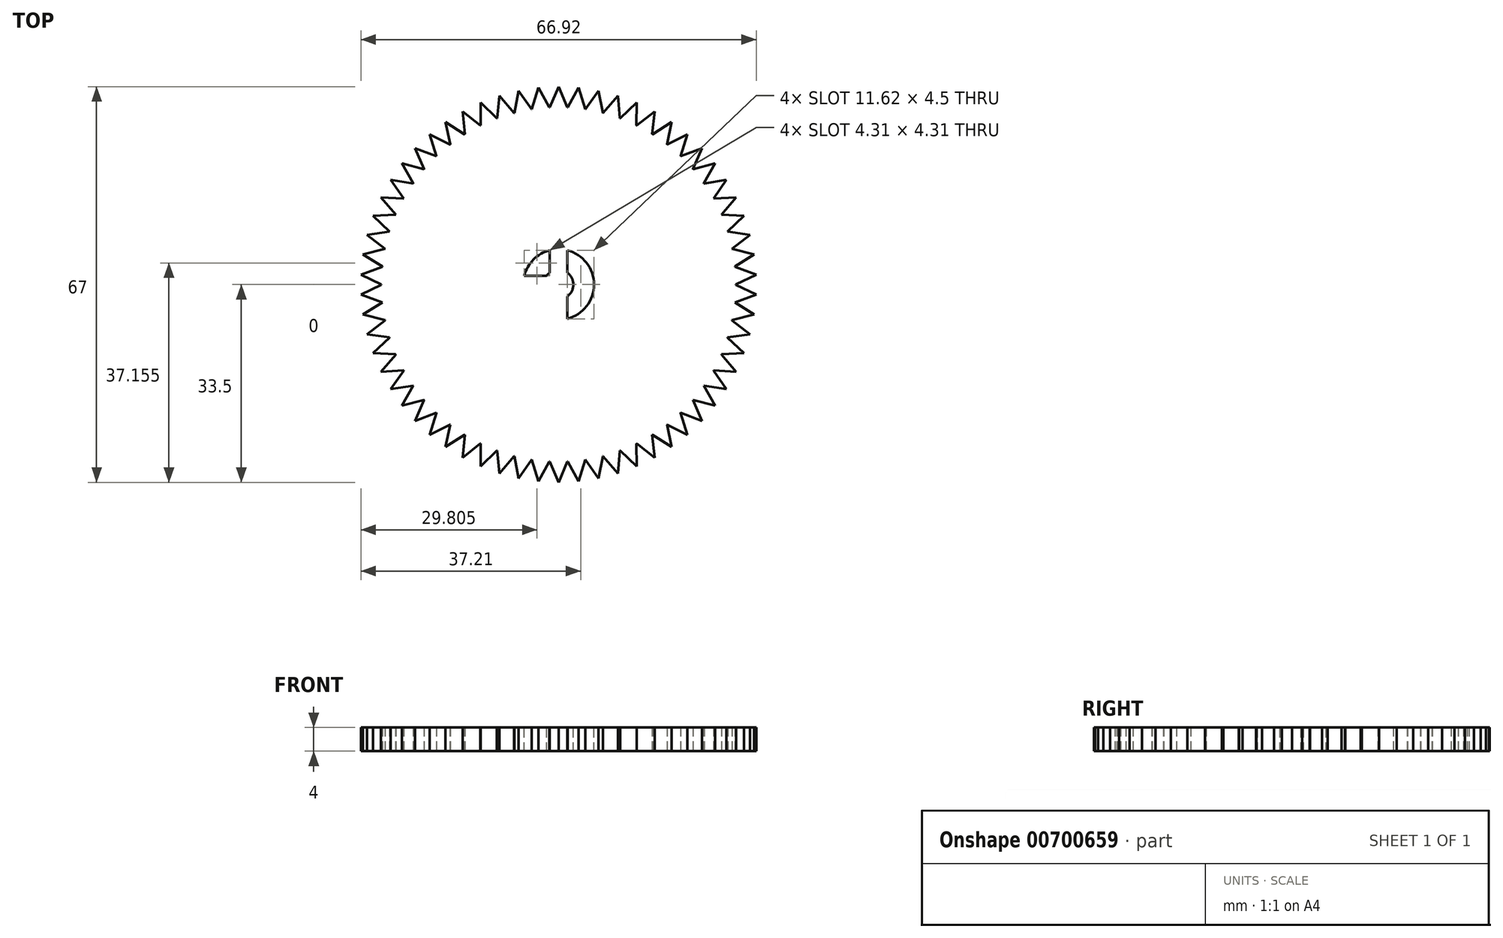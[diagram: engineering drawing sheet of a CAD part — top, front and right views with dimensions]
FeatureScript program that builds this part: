
annotation { "Feature Type Name" : "Feature", "Feature Type Description" : "" }
export const myFeature = defineFeature(function(context is Context, id is Id, definition is map)
    precondition{}
    {
        {
            var Q0;
            Q0=qCreatedBy(makeId("Top.planeOp"),FACE);
            var sketch = newSketch(context, id + "F0", { "sketchPlane" : qUnion([Q0])});
            skCircle(sketch, "E0", {"center": v(0, 0) * mm, "radius": 30 * mm});
            skLineSegment(sketch, "E1", {"start": v(0, 33.5) * mm, "end": v(-1.5, 29.96) * mm});
            skLineSegment(sketch, "E2", {"start": v(0, 33.5) * mm, "end": v(1.5, 29.96) * mm});
            skLineSegment(sketch, "E3.1.0", {"start": v(-3.39, 33.33) * mm, "end": v(-4.52, 29.66) * mm});
            skLineSegment(sketch, "E3.1.1", {"start": v(-3.39, 33.33) * mm, "end": v(-1.54, 29.96) * mm});
            skLineSegment(sketch, "E3.2.0", {"start": v(-6.74, 32.81) * mm, "end": v(-7.5, 29.05) * mm});
            skLineSegment(sketch, "E3.2.1", {"start": v(-6.74, 32.81) * mm, "end": v(-4.56, 29.65) * mm});
            skLineSegment(sketch, "E3.3.0", {"start": v(-10.03, 31.96) * mm, "end": v(-10.4, 28.14) * mm});
            skLineSegment(sketch, "E3.3.1", {"start": v(-10.03, 31.96) * mm, "end": v(-7.54, 29.04) * mm});
            skLineSegment(sketch, "E3.4.0", {"start": v(-13.21, 30.79) * mm, "end": v(-13.2, 26.94) * mm});
            skLineSegment(sketch, "E3.4.1", {"start": v(-13.21, 30.79) * mm, "end": v(-10.44, 28.13) * mm});
            skLineSegment(sketch, "E3.5.0", {"start": v(-16.26, 29.3) * mm, "end": v(-15.85, 25.47) * mm});
            skLineSegment(sketch, "E3.5.1", {"start": v(-16.26, 29.3) * mm, "end": v(-13.23, 26.93) * mm});
            skLineSegment(sketch, "E3.6.0", {"start": v(-19.14, 27.5) * mm, "end": v(-18.35, 23.74) * mm});
            skLineSegment(sketch, "E3.6.1", {"start": v(-19.14, 27.5) * mm, "end": v(-15.89, 25.45) * mm});
            skLineSegment(sketch, "E3.7.0", {"start": v(-21.82, 25.42) * mm, "end": v(-20.65, 21.76) * mm});
            skLineSegment(sketch, "E3.7.1", {"start": v(-21.82, 25.42) * mm, "end": v(-18.38, 23.71) * mm});
            skLineSegment(sketch, "E3.8.0", {"start": v(-24.28, 23.08) * mm, "end": v(-22.75, 19.56) * mm});
            skLineSegment(sketch, "E3.8.1", {"start": v(-24.28, 23.08) * mm, "end": v(-20.68, 21.73) * mm});
            skLineSegment(sketch, "E3.9.0", {"start": v(-26.5, 20.5) * mm, "end": v(-24.61, 17.15) * mm});
            skLineSegment(sketch, "E3.9.1", {"start": v(-26.5, 20.5) * mm, "end": v(-22.78, 19.53) * mm});
            skLineSegment(sketch, "E3.10.0", {"start": v(-28.43, 17.72) * mm, "end": v(-26.22, 14.58) * mm});
            skLineSegment(sketch, "E3.10.1", {"start": v(-28.43, 17.72) * mm, "end": v(-24.63, 17.12) * mm});
            skLineSegment(sketch, "E3.11.0", {"start": v(-30.08, 14.75) * mm, "end": v(-27.56, 11.85) * mm});
            skLineSegment(sketch, "E3.11.1", {"start": v(-30.08, 14.75) * mm, "end": v(-26.24, 14.54) * mm});
            skLineSegment(sketch, "E3.12.0", {"start": v(-31.41, 11.63) * mm, "end": v(-28.62, 9) * mm});
            skLineSegment(sketch, "E3.12.1", {"start": v(-31.41, 11.63) * mm, "end": v(-27.58, 11.81) * mm});
            skLineSegment(sketch, "E3.13.0", {"start": v(-32.43, 8.4) * mm, "end": v(-29.38, 6.06) * mm});
            skLineSegment(sketch, "E3.13.1", {"start": v(-32.43, 8.4) * mm, "end": v(-28.63, 8.96) * mm});
            skLineSegment(sketch, "E3.14.0", {"start": v(-33.11, 5.07) * mm, "end": v(-29.84, 3.05) * mm});
            skLineSegment(sketch, "E3.14.1", {"start": v(-33.11, 5.07) * mm, "end": v(-29.39, 6.02) * mm});
            skLineSegment(sketch, "E3.15.0", {"start": v(-33.46, 1.7) * mm, "end": v(-30, 0.02) * mm});
            skLineSegment(sketch, "E3.15.1", {"start": v(-33.46, 1.7) * mm, "end": v(-29.85, 3.02) * mm});
            skLineSegment(sketch, "E3.16.0", {"start": v(-33.46, -1.7) * mm, "end": v(-29.85, -3.02) * mm});
            skLineSegment(sketch, "E3.16.1", {"start": v(-33.46, -1.7) * mm, "end": v(-30, -0.02) * mm});
            skLineSegment(sketch, "E3.17.0", {"start": v(-33.11, -5.07) * mm, "end": v(-29.39, -6.02) * mm});
            skLineSegment(sketch, "E3.17.1", {"start": v(-33.11, -5.07) * mm, "end": v(-29.84, -3.05) * mm});
            skLineSegment(sketch, "E3.18.0", {"start": v(-32.43, -8.4) * mm, "end": v(-28.63, -8.96) * mm});
            skLineSegment(sketch, "E3.18.1", {"start": v(-32.43, -8.4) * mm, "end": v(-29.38, -6.06) * mm});
            skLineSegment(sketch, "E3.19.0", {"start": v(-31.41, -11.63) * mm, "end": v(-27.58, -11.81) * mm});
            skLineSegment(sketch, "E3.19.1", {"start": v(-31.41, -11.63) * mm, "end": v(-28.62, -9) * mm});
            skLineSegment(sketch, "E3.20.0", {"start": v(-30.08, -14.75) * mm, "end": v(-26.24, -14.54) * mm});
            skLineSegment(sketch, "E3.20.1", {"start": v(-30.08, -14.75) * mm, "end": v(-27.56, -11.85) * mm});
            skLineSegment(sketch, "E3.21.0", {"start": v(-28.43, -17.72) * mm, "end": v(-24.63, -17.12) * mm});
            skLineSegment(sketch, "E3.21.1", {"start": v(-28.43, -17.72) * mm, "end": v(-26.22, -14.58) * mm});
            skLineSegment(sketch, "E3.22.0", {"start": v(-26.5, -20.5) * mm, "end": v(-22.78, -19.53) * mm});
            skLineSegment(sketch, "E3.22.1", {"start": v(-26.5, -20.5) * mm, "end": v(-24.61, -17.15) * mm});
            skLineSegment(sketch, "E3.23.0", {"start": v(-24.28, -23.08) * mm, "end": v(-20.68, -21.73) * mm});
            skLineSegment(sketch, "E3.23.1", {"start": v(-24.28, -23.08) * mm, "end": v(-22.75, -19.56) * mm});
            skLineSegment(sketch, "E3.24.0", {"start": v(-21.82, -25.42) * mm, "end": v(-18.38, -23.71) * mm});
            skLineSegment(sketch, "E3.24.1", {"start": v(-21.82, -25.42) * mm, "end": v(-20.65, -21.76) * mm});
            skLineSegment(sketch, "E3.25.0", {"start": v(-19.14, -27.5) * mm, "end": v(-15.89, -25.45) * mm});
            skLineSegment(sketch, "E3.25.1", {"start": v(-19.14, -27.5) * mm, "end": v(-18.35, -23.74) * mm});
            skLineSegment(sketch, "E3.26.0", {"start": v(-16.26, -29.3) * mm, "end": v(-13.23, -26.93) * mm});
            skLineSegment(sketch, "E3.26.1", {"start": v(-16.26, -29.3) * mm, "end": v(-15.85, -25.47) * mm});
            skLineSegment(sketch, "E3.27.0", {"start": v(-13.21, -30.79) * mm, "end": v(-10.44, -28.13) * mm});
            skLineSegment(sketch, "E3.27.1", {"start": v(-13.21, -30.79) * mm, "end": v(-13.2, -26.94) * mm});
            skLineSegment(sketch, "E3.28.0", {"start": v(-10.03, -31.96) * mm, "end": v(-7.54, -29.04) * mm});
            skLineSegment(sketch, "E3.28.1", {"start": v(-10.03, -31.96) * mm, "end": v(-10.4, -28.14) * mm});
            skLineSegment(sketch, "E3.29.0", {"start": v(-6.74, -32.81) * mm, "end": v(-4.56, -29.65) * mm});
            skLineSegment(sketch, "E3.29.1", {"start": v(-6.74, -32.81) * mm, "end": v(-7.5, -29.05) * mm});
            skLineSegment(sketch, "E3.30.0", {"start": v(-3.39, -33.33) * mm, "end": v(-1.54, -29.96) * mm});
            skLineSegment(sketch, "E3.30.1", {"start": v(-3.39, -33.33) * mm, "end": v(-4.52, -29.66) * mm});
            skLineSegment(sketch, "E3.31.0", {"start": v(0, -33.5) * mm, "end": v(1.5, -29.96) * mm});
            skLineSegment(sketch, "E3.31.1", {"start": v(0, -33.5) * mm, "end": v(-1.5, -29.96) * mm});
            skLineSegment(sketch, "E3.32.0", {"start": v(3.39, -33.33) * mm, "end": v(4.52, -29.66) * mm});
            skLineSegment(sketch, "E3.32.1", {"start": v(3.39, -33.33) * mm, "end": v(1.54, -29.96) * mm});
            skLineSegment(sketch, "E3.33.0", {"start": v(6.74, -32.81) * mm, "end": v(7.5, -29.05) * mm});
            skLineSegment(sketch, "E3.33.1", {"start": v(6.74, -32.81) * mm, "end": v(4.56, -29.65) * mm});
            skLineSegment(sketch, "E3.34.0", {"start": v(10.03, -31.96) * mm, "end": v(10.4, -28.14) * mm});
            skLineSegment(sketch, "E3.34.1", {"start": v(10.03, -31.96) * mm, "end": v(7.54, -29.04) * mm});
            skLineSegment(sketch, "E3.35.0", {"start": v(13.21, -30.79) * mm, "end": v(13.2, -26.94) * mm});
            skLineSegment(sketch, "E3.35.1", {"start": v(13.21, -30.79) * mm, "end": v(10.44, -28.13) * mm});
            skLineSegment(sketch, "E3.36.0", {"start": v(16.26, -29.3) * mm, "end": v(15.85, -25.47) * mm});
            skLineSegment(sketch, "E3.36.1", {"start": v(16.26, -29.3) * mm, "end": v(13.23, -26.93) * mm});
            skLineSegment(sketch, "E3.37.0", {"start": v(19.14, -27.5) * mm, "end": v(18.35, -23.74) * mm});
            skLineSegment(sketch, "E3.37.1", {"start": v(19.14, -27.5) * mm, "end": v(15.89, -25.45) * mm});
            skLineSegment(sketch, "E3.38.0", {"start": v(21.82, -25.42) * mm, "end": v(20.65, -21.76) * mm});
            skLineSegment(sketch, "E3.38.1", {"start": v(21.82, -25.42) * mm, "end": v(18.38, -23.71) * mm});
            skLineSegment(sketch, "E3.39.0", {"start": v(24.28, -23.08) * mm, "end": v(22.75, -19.56) * mm});
            skLineSegment(sketch, "E3.39.1", {"start": v(24.28, -23.08) * mm, "end": v(20.68, -21.73) * mm});
            skLineSegment(sketch, "E3.40.0", {"start": v(26.5, -20.5) * mm, "end": v(24.61, -17.15) * mm});
            skLineSegment(sketch, "E3.40.1", {"start": v(26.5, -20.5) * mm, "end": v(22.78, -19.53) * mm});
            skLineSegment(sketch, "E3.41.0", {"start": v(28.43, -17.72) * mm, "end": v(26.22, -14.58) * mm});
            skLineSegment(sketch, "E3.41.1", {"start": v(28.43, -17.72) * mm, "end": v(24.63, -17.12) * mm});
            skLineSegment(sketch, "E3.42.0", {"start": v(30.08, -14.75) * mm, "end": v(27.56, -11.85) * mm});
            skLineSegment(sketch, "E3.42.1", {"start": v(30.08, -14.75) * mm, "end": v(26.24, -14.54) * mm});
            skLineSegment(sketch, "E3.43.0", {"start": v(31.41, -11.63) * mm, "end": v(28.62, -9) * mm});
            skLineSegment(sketch, "E3.43.1", {"start": v(31.41, -11.63) * mm, "end": v(27.58, -11.81) * mm});
            skLineSegment(sketch, "E3.44.0", {"start": v(32.43, -8.4) * mm, "end": v(29.38, -6.06) * mm});
            skLineSegment(sketch, "E3.44.1", {"start": v(32.43, -8.4) * mm, "end": v(28.63, -8.96) * mm});
            skLineSegment(sketch, "E3.45.0", {"start": v(33.11, -5.07) * mm, "end": v(29.84, -3.05) * mm});
            skLineSegment(sketch, "E3.45.1", {"start": v(33.11, -5.07) * mm, "end": v(29.39, -6.02) * mm});
            skLineSegment(sketch, "E3.46.0", {"start": v(33.46, -1.7) * mm, "end": v(30, -0.02) * mm});
            skLineSegment(sketch, "E3.46.1", {"start": v(33.46, -1.7) * mm, "end": v(29.85, -3.02) * mm});
            skLineSegment(sketch, "E3.47.0", {"start": v(33.46, 1.7) * mm, "end": v(29.85, 3.02) * mm});
            skLineSegment(sketch, "E3.47.1", {"start": v(33.46, 1.7) * mm, "end": v(30, 0.02) * mm});
            skLineSegment(sketch, "E3.48.0", {"start": v(33.11, 5.07) * mm, "end": v(29.39, 6.02) * mm});
            skLineSegment(sketch, "E3.48.1", {"start": v(33.11, 5.07) * mm, "end": v(29.84, 3.05) * mm});
            skLineSegment(sketch, "E3.49.0", {"start": v(32.43, 8.4) * mm, "end": v(28.63, 8.96) * mm});
            skLineSegment(sketch, "E3.49.1", {"start": v(32.43, 8.4) * mm, "end": v(29.38, 6.06) * mm});
            skLineSegment(sketch, "E3.50.0", {"start": v(31.41, 11.63) * mm, "end": v(27.58, 11.81) * mm});
            skLineSegment(sketch, "E3.50.1", {"start": v(31.41, 11.63) * mm, "end": v(28.62, 9) * mm});
            skLineSegment(sketch, "E3.51.0", {"start": v(30.08, 14.75) * mm, "end": v(26.24, 14.54) * mm});
            skLineSegment(sketch, "E3.51.1", {"start": v(30.08, 14.75) * mm, "end": v(27.56, 11.85) * mm});
            skLineSegment(sketch, "E3.52.0", {"start": v(28.43, 17.72) * mm, "end": v(24.63, 17.12) * mm});
            skLineSegment(sketch, "E3.52.1", {"start": v(28.43, 17.72) * mm, "end": v(26.22, 14.58) * mm});
            skLineSegment(sketch, "E3.53.0", {"start": v(26.5, 20.5) * mm, "end": v(22.78, 19.53) * mm});
            skLineSegment(sketch, "E3.53.1", {"start": v(26.5, 20.5) * mm, "end": v(24.61, 17.15) * mm});
            skLineSegment(sketch, "E3.54.0", {"start": v(24.28, 23.08) * mm, "end": v(20.68, 21.73) * mm});
            skLineSegment(sketch, "E3.54.1", {"start": v(24.28, 23.08) * mm, "end": v(22.75, 19.56) * mm});
            skLineSegment(sketch, "E3.55.0", {"start": v(21.82, 25.42) * mm, "end": v(18.38, 23.71) * mm});
            skLineSegment(sketch, "E3.55.1", {"start": v(21.82, 25.42) * mm, "end": v(20.65, 21.76) * mm});
            skLineSegment(sketch, "E3.56.0", {"start": v(19.14, 27.5) * mm, "end": v(15.89, 25.45) * mm});
            skLineSegment(sketch, "E3.56.1", {"start": v(19.14, 27.5) * mm, "end": v(18.35, 23.74) * mm});
            skLineSegment(sketch, "E3.57.0", {"start": v(16.26, 29.3) * mm, "end": v(13.23, 26.93) * mm});
            skLineSegment(sketch, "E3.57.1", {"start": v(16.26, 29.3) * mm, "end": v(15.85, 25.47) * mm});
            skLineSegment(sketch, "E3.58.0", {"start": v(13.21, 30.79) * mm, "end": v(10.44, 28.13) * mm});
            skLineSegment(sketch, "E3.58.1", {"start": v(13.21, 30.79) * mm, "end": v(13.2, 26.94) * mm});
            skLineSegment(sketch, "E3.59.0", {"start": v(10.03, 31.96) * mm, "end": v(7.54, 29.04) * mm});
            skLineSegment(sketch, "E3.59.1", {"start": v(10.03, 31.96) * mm, "end": v(10.4, 28.14) * mm});
            skLineSegment(sketch, "E3.60.0", {"start": v(6.74, 32.81) * mm, "end": v(4.56, 29.65) * mm});
            skLineSegment(sketch, "E3.60.1", {"start": v(6.74, 32.81) * mm, "end": v(7.5, 29.05) * mm});
            skLineSegment(sketch, "E3.61.0", {"start": v(3.39, 33.33) * mm, "end": v(1.54, 29.96) * mm});
            skLineSegment(sketch, "E3.61.1", {"start": v(3.39, 33.33) * mm, "end": v(4.52, 29.66) * mm});
            skSolve(sketch);
        }
        {
            var Q0;
            Q0 = qSketchRegion(id + "F0", true);
            extrude(context, id + "F1", {"entities" : qUnion([Q0]), "depth" : 4 * mm, "offsetDistance" : 25 * mm});
        }
        {
            var Q0;
            Q0=makeQuery(id+"F1.opExtrude","CAP_FACE",FACE,{"disambiguationData":[OSD([sQuery(id+"F0.wireOp",EDGE,"E0"),sQuery(id+"F0.wireOp",EDGE,"E1"),sQuery(id+"F0.wireOp",EDGE,"E2"),sQuery(id+"F0.wireOp",EDGE,"E3.1.0"),sQuery(id+"F0.wireOp",EDGE,"E3.1.1"),sQuery(id+"F0.wireOp",EDGE,"E3.2.0"),sQuery(id+"F0.wireOp",EDGE,"E3.2.1"),sQuery(id+"F0.wireOp",EDGE,"E3.3.0"),sQuery(id+"F0.wireOp",EDGE,"E3.3.1"),sQuery(id+"F0.wireOp",EDGE,"E3.4.0"),sQuery(id+"F0.wireOp",EDGE,"E3.4.1"),sQuery(id+"F0.wireOp",EDGE,"E3.5.0"),sQuery(id+"F0.wireOp",EDGE,"E3.5.1"),sQuery(id+"F0.wireOp",EDGE,"E3.6.0"),sQuery(id+"F0.wireOp",EDGE,"E3.6.1"),sQuery(id+"F0.wireOp",EDGE,"E3.7.0"),sQuery(id+"F0.wireOp",EDGE,"E3.7.1"),sQuery(id+"F0.wireOp",EDGE,"E3.8.0"),sQuery(id+"F0.wireOp",EDGE,"E3.8.1"),sQuery(id+"F0.wireOp",EDGE,"E3.9.0"),sQuery(id+"F0.wireOp",EDGE,"E3.9.1"),sQuery(id+"F0.wireOp",EDGE,"E3.10.0"),sQuery(id+"F0.wireOp",EDGE,"E3.10.1"),sQuery(id+"F0.wireOp",EDGE,"E3.11.0"),sQuery(id+"F0.wireOp",EDGE,"E3.11.1"),sQuery(id+"F0.wireOp",EDGE,"E3.12.0"),sQuery(id+"F0.wireOp",EDGE,"E3.12.1"),sQuery(id+"F0.wireOp",EDGE,"E3.13.0"),sQuery(id+"F0.wireOp",EDGE,"E3.13.1"),sQuery(id+"F0.wireOp",EDGE,"E3.14.0"),sQuery(id+"F0.wireOp",EDGE,"E3.14.1"),sQuery(id+"F0.wireOp",EDGE,"E3.15.0"),sQuery(id+"F0.wireOp",EDGE,"E3.15.1"),sQuery(id+"F0.wireOp",EDGE,"E3.16.0"),sQuery(id+"F0.wireOp",EDGE,"E3.16.1"),sQuery(id+"F0.wireOp",EDGE,"E3.17.0"),sQuery(id+"F0.wireOp",EDGE,"E3.17.1"),sQuery(id+"F0.wireOp",EDGE,"E3.18.0"),sQuery(id+"F0.wireOp",EDGE,"E3.18.1"),sQuery(id+"F0.wireOp",EDGE,"E3.19.0"),sQuery(id+"F0.wireOp",EDGE,"E3.19.1"),sQuery(id+"F0.wireOp",EDGE,"E3.20.0"),sQuery(id+"F0.wireOp",EDGE,"E3.20.1"),sQuery(id+"F0.wireOp",EDGE,"E3.21.0"),sQuery(id+"F0.wireOp",EDGE,"E3.21.1"),sQuery(id+"F0.wireOp",EDGE,"E3.22.0"),sQuery(id+"F0.wireOp",EDGE,"E3.22.1"),sQuery(id+"F0.wireOp",EDGE,"E3.23.0"),sQuery(id+"F0.wireOp",EDGE,"E3.23.1"),sQuery(id+"F0.wireOp",EDGE,"E3.24.0"),sQuery(id+"F0.wireOp",EDGE,"E3.24.1"),sQuery(id+"F0.wireOp",EDGE,"E3.25.0"),sQuery(id+"F0.wireOp",EDGE,"E3.25.1"),sQuery(id+"F0.wireOp",EDGE,"E3.26.0"),sQuery(id+"F0.wireOp",EDGE,"E3.26.1"),sQuery(id+"F0.wireOp",EDGE,"E3.27.0"),sQuery(id+"F0.wireOp",EDGE,"E3.27.1"),sQuery(id+"F0.wireOp",EDGE,"E3.28.0"),sQuery(id+"F0.wireOp",EDGE,"E3.28.1"),sQuery(id+"F0.wireOp",EDGE,"E3.29.0"),sQuery(id+"F0.wireOp",EDGE,"E3.29.1"),sQuery(id+"F0.wireOp",EDGE,"E3.30.0"),sQuery(id+"F0.wireOp",EDGE,"E3.30.1"),sQuery(id+"F0.wireOp",EDGE,"E3.31.0"),sQuery(id+"F0.wireOp",EDGE,"E3.31.1"),sQuery(id+"F0.wireOp",EDGE,"E3.32.0"),sQuery(id+"F0.wireOp",EDGE,"E3.32.1"),sQuery(id+"F0.wireOp",EDGE,"E3.33.0"),sQuery(id+"F0.wireOp",EDGE,"E3.33.1"),sQuery(id+"F0.wireOp",EDGE,"E3.34.0"),sQuery(id+"F0.wireOp",EDGE,"E3.34.1"),sQuery(id+"F0.wireOp",EDGE,"E3.35.0"),sQuery(id+"F0.wireOp",EDGE,"E3.35.1"),sQuery(id+"F0.wireOp",EDGE,"E3.36.0"),sQuery(id+"F0.wireOp",EDGE,"E3.36.1"),sQuery(id+"F0.wireOp",EDGE,"E3.37.0"),sQuery(id+"F0.wireOp",EDGE,"E3.37.1"),sQuery(id+"F0.wireOp",EDGE,"E3.38.0"),sQuery(id+"F0.wireOp",EDGE,"E3.38.1"),sQuery(id+"F0.wireOp",EDGE,"E3.39.0"),sQuery(id+"F0.wireOp",EDGE,"E3.39.1"),sQuery(id+"F0.wireOp",EDGE,"E3.40.0"),sQuery(id+"F0.wireOp",EDGE,"E3.40.1"),sQuery(id+"F0.wireOp",EDGE,"E3.41.0"),sQuery(id+"F0.wireOp",EDGE,"E3.41.1"),sQuery(id+"F0.wireOp",EDGE,"E3.42.0"),sQuery(id+"F0.wireOp",EDGE,"E3.42.1"),sQuery(id+"F0.wireOp",EDGE,"E3.43.0"),sQuery(id+"F0.wireOp",EDGE,"E3.43.1"),sQuery(id+"F0.wireOp",EDGE,"E3.44.0"),sQuery(id+"F0.wireOp",EDGE,"E3.44.1"),sQuery(id+"F0.wireOp",EDGE,"E3.45.0"),sQuery(id+"F0.wireOp",EDGE,"E3.45.1"),sQuery(id+"F0.wireOp",EDGE,"E3.46.0"),sQuery(id+"F0.wireOp",EDGE,"E3.46.1"),sQuery(id+"F0.wireOp",EDGE,"E3.47.0"),sQuery(id+"F0.wireOp",EDGE,"E3.47.1"),sQuery(id+"F0.wireOp",EDGE,"E3.48.0"),sQuery(id+"F0.wireOp",EDGE,"E3.48.1"),sQuery(id+"F0.wireOp",EDGE,"E3.49.0"),sQuery(id+"F0.wireOp",EDGE,"E3.49.1"),sQuery(id+"F0.wireOp",EDGE,"E3.50.0"),sQuery(id+"F0.wireOp",EDGE,"E3.50.1"),sQuery(id+"F0.wireOp",EDGE,"E3.51.0"),sQuery(id+"F0.wireOp",EDGE,"E3.51.1"),sQuery(id+"F0.wireOp",EDGE,"E3.52.0"),sQuery(id+"F0.wireOp",EDGE,"E3.52.1"),sQuery(id+"F0.wireOp",EDGE,"E3.53.0"),sQuery(id+"F0.wireOp",EDGE,"E3.53.1"),sQuery(id+"F0.wireOp",EDGE,"E3.54.0"),sQuery(id+"F0.wireOp",EDGE,"E3.54.1"),sQuery(id+"F0.wireOp",EDGE,"E3.55.0"),sQuery(id+"F0.wireOp",EDGE,"E3.55.1"),sQuery(id+"F0.wireOp",EDGE,"E3.56.0"),sQuery(id+"F0.wireOp",EDGE,"E3.56.1"),sQuery(id+"F0.wireOp",EDGE,"E3.57.0"),sQuery(id+"F0.wireOp",EDGE,"E3.57.1"),sQuery(id+"F0.wireOp",EDGE,"E3.58.0"),sQuery(id+"F0.wireOp",EDGE,"E3.58.1"),sQuery(id+"F0.wireOp",EDGE,"E3.59.0"),sQuery(id+"F0.wireOp",EDGE,"E3.59.1"),sQuery(id+"F0.wireOp",EDGE,"E3.60.0"),sQuery(id+"F0.wireOp",EDGE,"E3.60.1"),sQuery(id+"F0.wireOp",EDGE,"E3.61.0"),sQuery(id+"F0.wireOp",EDGE,"E3.61.1")])],"isStart":false});
            var sketch = newSketch(context, id + "F2", { "sketchPlane" : qUnion([Q0])});
            skCircle(sketch, "E4", {"center": v(0, 0) * mm, "radius": 6 * mm});
            skLineSegment(sketch, "E5.bottom", {"start": v(1.5, 7.14) * mm, "end": v(-1.5, 7.14) * mm});
            skLineSegment(sketch, "E5.top", {"start": v(1.5, -7.14) * mm, "end": v(-1.5, -7.14) * mm});
            skLineSegment(sketch, "E5.left", {"start": v(1.5, 7.14) * mm, "end": v(1.5, -7.14) * mm});
            skLineSegment(sketch, "E5.right", {"start": v(-1.5, 7.14) * mm, "end": v(-1.5, -7.14) * mm});
            skLineSegment(sketch, "E6.bottom", {"start": v(8.52, 1.5) * mm, "end": v(-8.52, 1.5) * mm});
            skLineSegment(sketch, "E6.top", {"start": v(8.52, -1.5) * mm, "end": v(-8.52, -1.5) * mm});
            skLineSegment(sketch, "E6.left", {"start": v(8.52, 1.5) * mm, "end": v(8.52, -1.5) * mm});
            skLineSegment(sketch, "E6.right", {"start": v(-8.52, 1.5) * mm, "end": v(-8.52, -1.5) * mm});
            skCircle(sketch, "E7", {"center": v(0, 0) * mm, "radius": 2.5 * mm});
            skSolve(sketch);
        }
        {
            var Q0;
            {var subQ0=sQuery(id+"F2.wireOp",EDGE,"E5.right");var subQ1=sQuery(id+"F2.wireOp",EDGE,"E4");var subQ2=makeQuery(id+"F2.imprint","INTERSECT",VERTEX,{"disambiguationData":[OD(0.0)],"derivedFrom":[subQ1,subQ0]});Q0=makeQuery(id+"F2.imprint","IMPRINT",FACE,{"disambiguationData":[TD([[makeQuery(id+"F2.imprint","IMPRINT",EDGE,{"disambiguationData":[TD([[subQ2,-1.0]])],"derivedFrom":subQ1}),1.0]])]});}
            var Q1;
            {var subQ0=sQuery(id+"F2.wireOp",EDGE,"E5.left");var subQ1=sQuery(id+"F2.wireOp",EDGE,"E4");var subQ2=makeQuery(id+"F2.imprint","INTERSECT",VERTEX,{"disambiguationData":[OD(0.0)],"derivedFrom":[subQ1,subQ0]});Q1=makeQuery(id+"F2.imprint","IMPRINT",FACE,{"disambiguationData":[TD([[makeQuery(id+"F2.imprint","IMPRINT",EDGE,{"disambiguationData":[TD([[subQ2,1.0]])],"derivedFrom":subQ1}),1.0]])]});}
            var Q2;
            {var subQ0=sQuery(id+"F2.wireOp",EDGE,"E5.left");var subQ1=sQuery(id+"F2.wireOp",EDGE,"E4");var subQ2=makeQuery(id+"F2.imprint","INTERSECT",VERTEX,{"disambiguationData":[OD(1.0)],"derivedFrom":[subQ1,subQ0]});Q2=makeQuery(id+"F2.imprint","IMPRINT",FACE,{"disambiguationData":[TD([[makeQuery(id+"F2.imprint","IMPRINT",EDGE,{"disambiguationData":[TD([[subQ2,-1.0]])],"derivedFrom":subQ1}),1.0]])]});}
            var Q3;
            {var subQ0=sQuery(id+"F2.wireOp",EDGE,"E6.top");var subQ1=sQuery(id+"F2.wireOp",EDGE,"E4");var subQ2=makeQuery(id+"F2.imprint","INTERSECT",VERTEX,{"disambiguationData":[OD(0.0)],"derivedFrom":[subQ1,subQ0]});Q3=makeQuery(id+"F2.imprint","IMPRINT",FACE,{"disambiguationData":[TD([[makeQuery(id+"F2.imprint","IMPRINT",EDGE,{"disambiguationData":[TD([[subQ2,-1.0]])],"derivedFrom":subQ1}),1.0]])]});}
            extrude(context, id + "F3", {"entities" : qUnion([Q0, Q1, Q2, Q3]), "operationType" : NewBodyOperationType.REMOVE, "oppositeDirection" : true, "depth" : 4 * mm, "offsetDistance" : 25 * mm});
        }
    });
